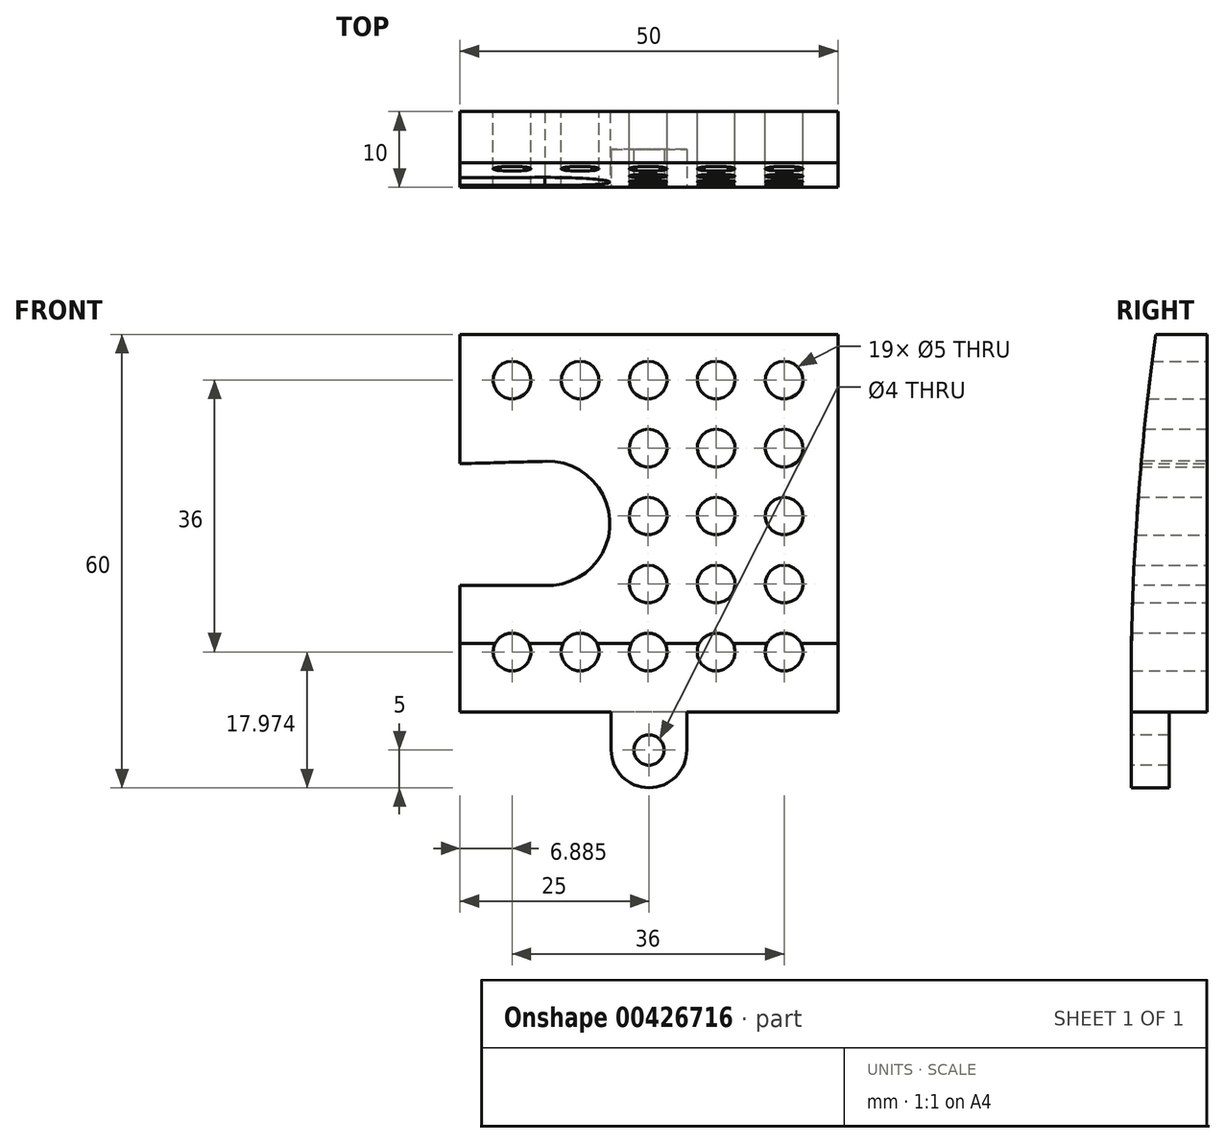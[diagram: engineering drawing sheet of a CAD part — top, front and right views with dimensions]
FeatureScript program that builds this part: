
annotation { "Feature Type Name" : "Feature", "Feature Type Description" : "" }
export const myFeature = defineFeature(function(context is Context, id is Id, definition is map)
    precondition{}
    {
        {
            var Q0;
            Q0=qCreatedBy(makeId("Front.planeOp"),FACE);
            var sketch = newSketch(context, id + "F0", { "sketchPlane" : qUnion([Q0])});
            skLineSegment(sketch, "E0.bottom", {"start": v(25, 25) * mm, "end": v(-25, 25) * mm});
            skLineSegment(sketch, "E0.top", {"start": v(25, -25) * mm, "end": v(-25, -25) * mm});
            skLineSegment(sketch, "E0.left", {"start": v(25, 25) * mm, "end": v(25, -25) * mm});
            skLineSegment(sketch, "E0.right", {"start": v(-25, 25) * mm, "end": v(-25, -25) * mm});
            skPoint(sketch, "E0.middle", {"position": v(0, 0) * mm});
            skSolve(sketch);
        }
        {
            var Q0;
            Q0 = qSketchRegion(id + "F0", true);
            extrude(context, id + "F1", {"entities" : qUnion([Q0]), "depth" : 10 * mm});
        }
        {
            var Q0;
            Q0=makeQuery(id+"F1.opExtrude","CAP_FACE",FACE,{"disambiguationData":[OSD([sQuery(id+"F0.wireOp",EDGE,"E0.bottom"),sQuery(id+"F0.wireOp",EDGE,"E0.top"),sQuery(id+"F0.wireOp",EDGE,"E0.left"),sQuery(id+"F0.wireOp",EDGE,"E0.right")])],"isStart":false});
            var sketch = newSketch(context, id + "F2", { "sketchPlane" : qUnion([Q0])});
            skArc(sketch, "E1", {"start": v(-13.78, -8.2) * mm, "mid": v(-5.17, -0.09) * mm, "end": v(-13.6, 8.21) * mm});
            skLineSegment(sketch, "E2", {"start": v(-13.78, -8.2) * mm, "end": v(-32.97, -8.2) * mm});
            skLineSegment(sketch, "E3", {"start": v(-32.97, -8.2) * mm, "end": v(-32.97, 7.69) * mm});
            skLineSegment(sketch, "E4", {"start": v(-32.97, 7.69) * mm, "end": v(-13.6, 8.21) * mm});
            skSolve(sketch);
        }
        {
            var Q0;
            Q0 = qSketchRegion(id + "F2", true);
            extrude(context, id + "F3", {"entities" : qUnion([Q0]), "operationType" : NewBodyOperationType.REMOVE, "oppositeDirection" : true, "depth" : 25 * mm});
        }
        {
            var Q0;
            {var subQ0=sQuery(id+"F0.wireOp",EDGE,"E0.bottom");var subQ1=sQuery(id+"F0.wireOp",EDGE,"E0.right");Q0=makeQuery(id+"F3.boolean.opBoolean","SPLIT",FACE,{"disambiguationData":[TD([makeQuery(id+"F1.opExtrude","SWEPT_FACE",FACE,{"disambiguationData":[OSD([subQ0])]})])],"derivedFrom":makeQuery(id+"F1.opExtrude","SWEPT_FACE",FACE,{"disambiguationData":[OSD([subQ1])]})});}
            var sketch = newSketch(context, id + "F4", { "sketchPlane" : qUnion([Q0])});
            skFitSpline(sketch, "E5", {"points": [v(10, -25) * mm, v(6.76, 25) * mm], "startDerivative": vector(0.97, 54.31) * mm, "endDerivative": vector(-5.54, 37.85) * mm});
            skLineSegment(sketch, "E6", {"start": v(6.76, 25) * mm, "end": v(14.14, 25) * mm});
            skLineSegment(sketch, "E7", {"start": v(14.14, 25) * mm, "end": v(10, -25) * mm});
            skSolve(sketch);
        }
        {
            var Q0;
            Q0 = qSketchRegion(id + "F4", true);
            extrude(context, id + "F5", {"entities" : qUnion([Q0]), "operationType" : NewBodyOperationType.REMOVE, "oppositeDirection" : true, "depth" : 51.8 * mm});
        }
        {
            var Q0;
            Q0=makeQuery(id+"F1.opExtrude","CAP_FACE",FACE,{"disambiguationData":[OSD([sQuery(id+"F0.wireOp",EDGE,"E0.bottom"),sQuery(id+"F0.wireOp",EDGE,"E0.top"),sQuery(id+"F0.wireOp",EDGE,"E0.left"),sQuery(id+"F0.wireOp",EDGE,"E0.right")])],"isStart":false});
            var sketch = newSketch(context, id + "F6", { "sketchPlane" : qUnion([Q0])});
            skLineSegment(sketch, "E8", {"start": v(0, -25) * mm, "end": v(0, -35) * mm, "construction": true});
            skLineSegment(sketch, "E9", {"start": v(0, -35) * mm, "end": v(0, -35) * mm});
            skLineSegment(sketch, "E10", {"start": v(-5, -30) * mm, "end": v(-5, -25) * mm});
            skLineSegment(sketch, "E11", {"start": v(-5, -25) * mm, "end": v(0, -25) * mm});
            skPoint(sketch, "E12.visualSharp", {"position": v(-5, -35) * mm});
            skArc(sketch, "E12.filletArc", {"start": v(-5, -30) * mm, "mid": v(-3.54, -33.54) * mm, "end": v(0, -35) * mm});
            skCircle(sketch, "E13", {"center": v(0, -30) * mm, "radius": 2 * mm});
            skLineSegment(sketch, "E14.MirrorCS", {"start": v(5, -25) * mm, "end": v(0, -25) * mm});
            skLineSegment(sketch, "E15.MirrorCS", {"start": v(5, -30) * mm, "end": v(5, -25) * mm});
            skArc(sketch, "E16.MirrorCS", {"start": v(5, -30) * mm, "mid": v(3.54, -33.54) * mm, "end": v(0, -35) * mm});
            skSolve(sketch);
        }
        {
            var Q0;
            Q0 = qSketchRegion(id + "F6", true);
            extrude(context, id + "F7", {"entities" : qUnion([Q0]), "operationType" : NewBodyOperationType.ADD, "oppositeDirection" : true, "depth" : 5 * mm});
        }
        {
            var Q0;
            Q0=makeQuery(id+"F1.opExtrude","CAP_FACE",FACE,{"disambiguationData":[OSD([sQuery(id+"F0.wireOp",EDGE,"E0.bottom"),sQuery(id+"F0.wireOp",EDGE,"E0.top"),sQuery(id+"F0.wireOp",EDGE,"E0.left"),sQuery(id+"F0.wireOp",EDGE,"E0.right")])],"isStart":true});
            var sketch = newSketch(context, id + "F8", { "sketchPlane" : qUnion([Q0])});
            skCircle(sketch, "E17", {"center": v(-17.89, 18.97) * mm, "radius": 2.5 * mm});
            skCircle(sketch, "E18.0.1.0", {"center": v(-17.89, 9.97) * mm, "radius": 2.5 * mm});
            skCircle(sketch, "E18.0.2.0", {"center": v(-17.89, 0.97) * mm, "radius": 2.5 * mm});
            skCircle(sketch, "E18.0.3.0", {"center": v(-17.89, -8.03) * mm, "radius": 2.5 * mm});
            skCircle(sketch, "E18.0.4.0", {"center": v(-17.89, -17.03) * mm, "radius": 2.5 * mm});
            skCircle(sketch, "E18.1.0.0", {"center": v(-8.89, 18.97) * mm, "radius": 2.5 * mm});
            skCircle(sketch, "E18.1.1.0", {"center": v(-8.89, 9.97) * mm, "radius": 2.5 * mm});
            skCircle(sketch, "E18.1.2.0", {"center": v(-8.89, 0.97) * mm, "radius": 2.5 * mm});
            skCircle(sketch, "E18.1.3.0", {"center": v(-8.89, -8.03) * mm, "radius": 2.5 * mm});
            skCircle(sketch, "E18.1.4.0", {"center": v(-8.89, -17.03) * mm, "radius": 2.5 * mm});
            skCircle(sketch, "E18.2.0.0", {"center": v(0.11, 18.97) * mm, "radius": 2.5 * mm});
            skCircle(sketch, "E18.2.1.0", {"center": v(0.11, 9.97) * mm, "radius": 2.5 * mm});
            skCircle(sketch, "E18.2.2.0", {"center": v(0.11, 0.97) * mm, "radius": 2.5 * mm});
            skCircle(sketch, "E18.2.3.0", {"center": v(0.11, -8.03) * mm, "radius": 2.5 * mm});
            skCircle(sketch, "E18.2.4.0", {"center": v(0.11, -17.03) * mm, "radius": 2.5 * mm});
            skCircle(sketch, "E18.3.0.0", {"center": v(9.11, 18.97) * mm, "radius": 2.5 * mm});
            skCircle(sketch, "E18.3.4.0", {"center": v(9.11, -17.03) * mm, "radius": 2.5 * mm});
            skCircle(sketch, "E18.4.0.0", {"center": v(18.11, 18.97) * mm, "radius": 2.5 * mm});
            skCircle(sketch, "E18.4.4.0", {"center": v(18.11, -17.03) * mm, "radius": 2.5 * mm});
            skLineSegment(sketch, "E18.direction1", {"start": v(-17.89, 18.97) * mm, "end": v(-8.89, 18.97) * mm, "construction": true});
            skLineSegment(sketch, "E18.direction2", {"start": v(-17.89, 18.97) * mm, "end": v(-17.89, 9.97) * mm, "construction": true});
            skSolve(sketch);
        }
        {
            var Q0;
            Q0 = qSketchRegion(id + "F8", true);
            extrude(context, id + "F9", {"entities" : qUnion([Q0]), "operationType" : NewBodyOperationType.REMOVE, "oppositeDirection" : true, "depth" : 25 * mm});
        }
    });
